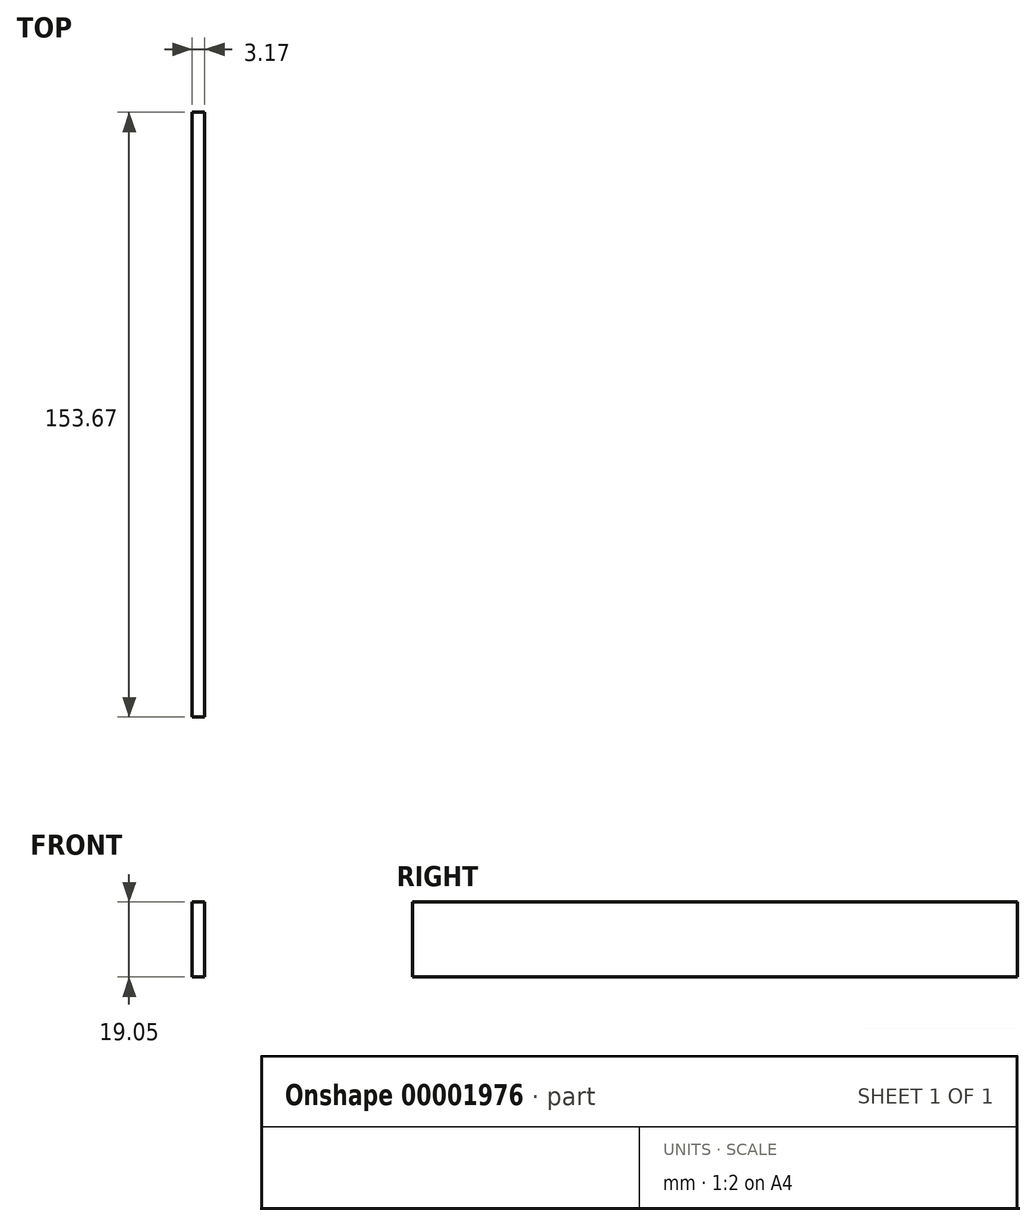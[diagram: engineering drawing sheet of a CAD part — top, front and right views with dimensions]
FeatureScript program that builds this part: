
annotation { "Feature Type Name" : "Feature", "Feature Type Description" : "" }
export const myFeature = defineFeature(function(context is Context, id is Id, definition is map)
    precondition{}
    {
        {
            var Q0;
            Q0=qCreatedBy(makeId("Right.planeOp"),FACE);
            var sketch = newSketch(context, id + "F0", { "sketchPlane" : qUnion([Q0])});
            skLineSegment(sketch, "E0.bottom", {"start": v(0, 0) * mm, "end": v(-153.67, 0) * mm});
            skLineSegment(sketch, "E0.top", {"start": v(0, 19.05) * mm, "end": v(-153.67, 19.05) * mm});
            skLineSegment(sketch, "E0.left", {"start": v(0, 0) * mm, "end": v(0, 19.05) * mm});
            skLineSegment(sketch, "E0.right", {"start": v(-153.67, 0) * mm, "end": v(-153.67, 19.05) * mm});
            skSolve(sketch);
        }
        {
            var Q0;
            Q0=makeQuery(id+"F0.imprint","IMPRINT",FACE,{"disambiguationData":[TD([[makeQuery(id+"F0.imprint","IMPRINT",EDGE,{"derivedFrom":sQuery(id+"F0.wireOp",EDGE,"E0.bottom")}),-1.0]])]});
            extrude(context, id + "F1", {"entities" : qUnion([Q0]), "depth" : 3.17 * mm});
        }
    });
